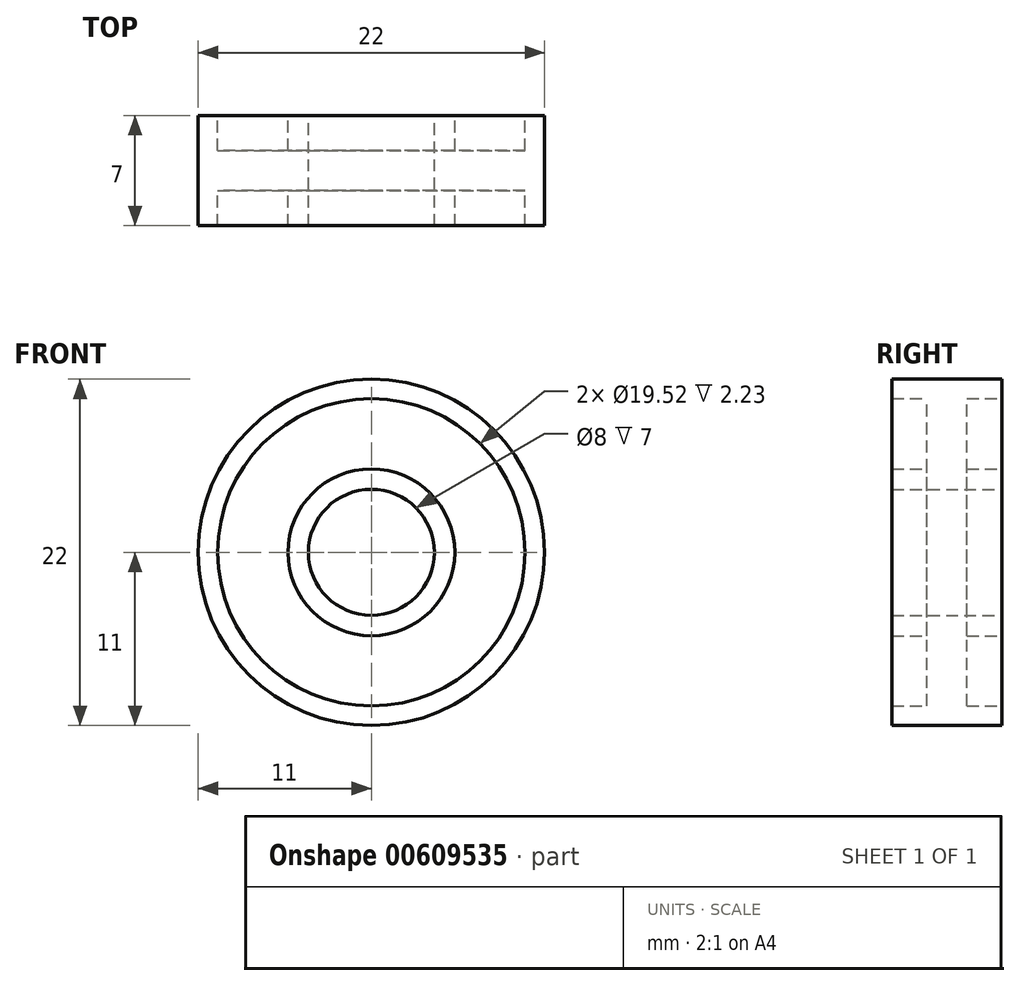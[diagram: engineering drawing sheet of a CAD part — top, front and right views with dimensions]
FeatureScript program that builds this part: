
annotation { "Feature Type Name" : "Feature", "Feature Type Description" : "" }
export const myFeature = defineFeature(function(context is Context, id is Id, definition is map)
    precondition{}
    {
        {
            var Q0;
            Q0=qCreatedBy(makeId("Front.planeOp"),FACE);
            var sketch = newSketch(context, id + "F0", { "sketchPlane" : qUnion([Q0])});
            skCircle(sketch, "E0", {"center": v(0, 0) * mm, "radius": 11 * mm});
            skCircle(sketch, "E1", {"center": v(0, 0) * mm, "radius": 9.76 * mm});
            skCircle(sketch, "E2", {"center": v(0, 0) * mm, "radius": 5.3 * mm});
            skCircle(sketch, "E3", {"center": v(0, 0) * mm, "radius": 4 * mm});
            skSolve(sketch);
        }
        {
            var Q0;
            Q0=makeQuery(id+"F0.imprint","IMPRINT",FACE,{"disambiguationData":[TD([[makeQuery(id+"F0.imprint","IMPRINT",EDGE,{"derivedFrom":sQuery(id+"F0.wireOp",EDGE,"E0")}),1.0]])]});
            var Q1;
            Q1=makeQuery(id+"F0.imprint","IMPRINT",FACE,{"disambiguationData":[TD([[makeQuery(id+"F0.imprint","IMPRINT",EDGE,{"derivedFrom":sQuery(id+"F0.wireOp",EDGE,"E2")}),1.0]])]});
            extrude(context, id + "F1", {"entities" : qUnion([Q0, Q1]), "endBound" : BoundingType.SYMMETRIC, "depth" : 7 * mm, "offsetDistance" : 25.4 * mm});
        }
        {
            var Q0;
            Q0=makeQuery(id+"F0.imprint","IMPRINT",FACE,{"disambiguationData":[TD([[makeQuery(id+"F0.imprint","IMPRINT",EDGE,{"derivedFrom":sQuery(id+"F0.wireOp",EDGE,"E1")}),1.0]])]});
            extrude(context, id + "F2", {"entities" : qUnion([Q0]), "operationType" : NewBodyOperationType.ADD, "endBound" : BoundingType.SYMMETRIC, "depth" : 2.54 * mm, "offsetDistance" : 25.4 * mm});
        }
    });
